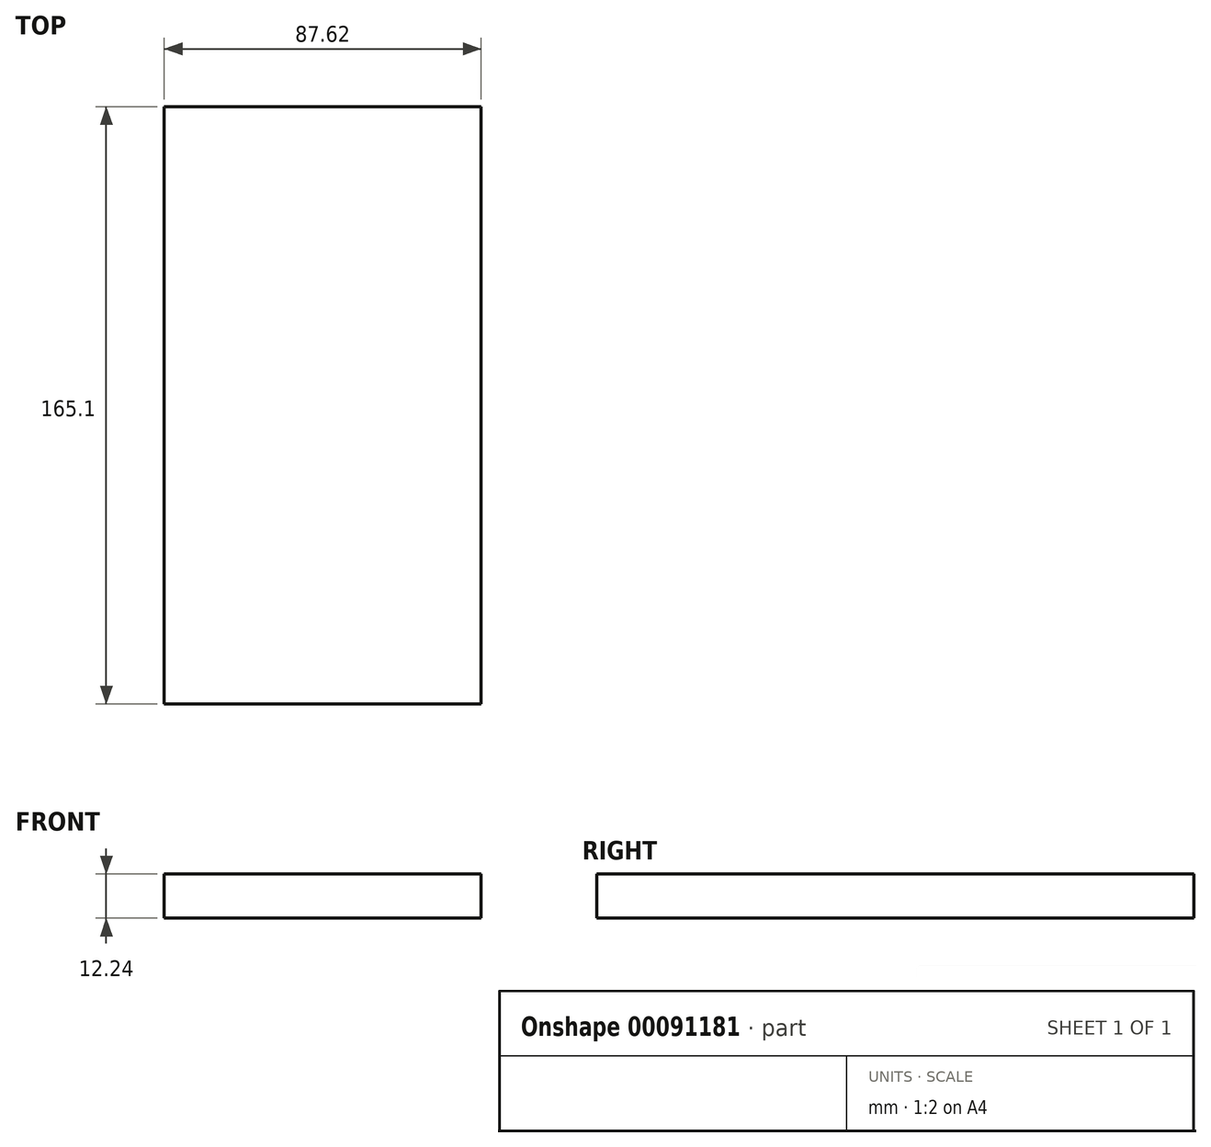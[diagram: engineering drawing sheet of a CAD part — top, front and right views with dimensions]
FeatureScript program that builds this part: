
annotation { "Feature Type Name" : "Feature", "Feature Type Description" : "" }
export const myFeature = defineFeature(function(context is Context, id is Id, definition is map)
    precondition{}
    {
        {
            var Q0;
            Q0=qCreatedBy(makeId("Top.planeOp"),FACE);
            var sketch = newSketch(context, id + "F0", { "sketchPlane" : qUnion([Q0])});
            skLineSegment(sketch, "E0.bottom", {"start": v(43.81, -82.55) * mm, "end": v(-43.82, -82.55) * mm});
            skLineSegment(sketch, "E0.top", {"start": v(43.82, 82.55) * mm, "end": v(-43.81, 82.55) * mm});
            skLineSegment(sketch, "E0.left", {"start": v(43.81, -82.55) * mm, "end": v(43.82, 82.55) * mm});
            skLineSegment(sketch, "E0.right", {"start": v(-43.82, -82.55) * mm, "end": v(-43.81, 82.55) * mm});
            skPoint(sketch, "E0.middle", {"position": v(0, 0) * mm});
            skSolve(sketch);
        }
        {
            var Q0;
            Q0 = qSketchRegion(id + "F0", true);
            extrude(context, id + "F1", {"entities" : qUnion([Q0]), "depth" : 12.24 * mm});
        }
    });
